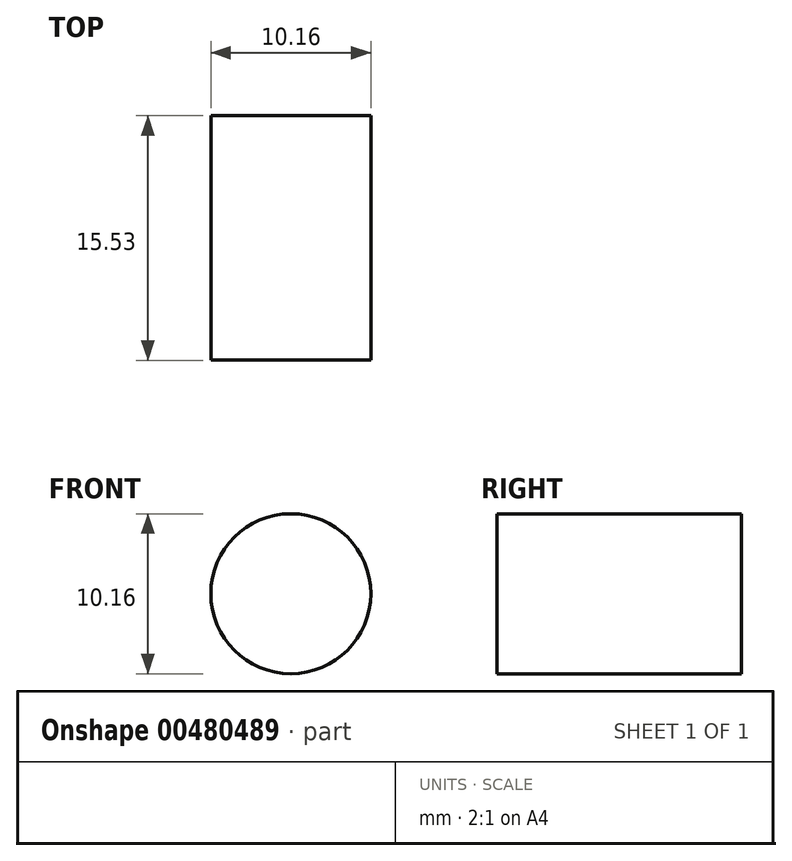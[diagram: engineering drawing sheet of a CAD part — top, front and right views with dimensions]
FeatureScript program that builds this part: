
annotation { "Feature Type Name" : "Feature", "Feature Type Description" : "" }
export const myFeature = defineFeature(function(context is Context, id is Id, definition is map)
    precondition{}
    {
        {
            var Q0;
            Q0=qCreatedBy(makeId("Front.planeOp"),FACE);
            var sketch = newSketch(context, id + "F0", { "sketchPlane" : qUnion([Q0])});
            skCircle(sketch, "E0", {"center": v(0, 0) * mm, "radius": 5.08 * mm});
            skSolve(sketch);
        }
        {
            var Q0;
            Q0 = qSketchRegion(id + "F0", true);
            extrude(context, id + "F1", {"entities" : qUnion([Q0]), "depth" : 15.53 * mm});
        }
    });
